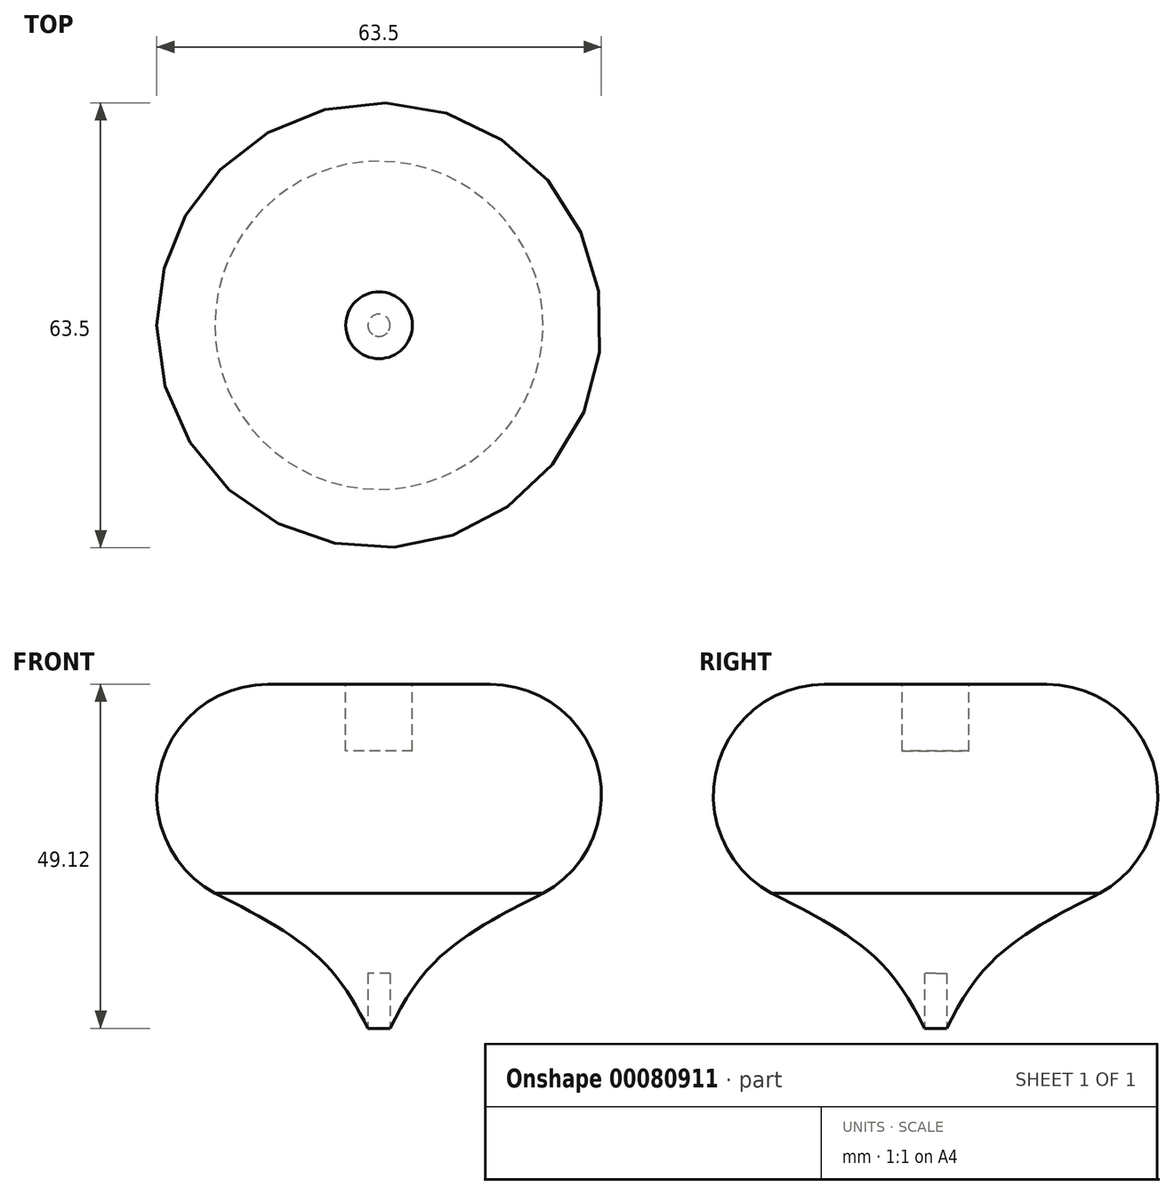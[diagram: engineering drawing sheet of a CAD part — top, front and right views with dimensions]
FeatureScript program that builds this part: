
annotation { "Feature Type Name" : "Feature", "Feature Type Description" : "" }
export const myFeature = defineFeature(function(context is Context, id is Id, definition is map)
    precondition{}
    {
        {
            var Q0;
            Q0=qCreatedBy(makeId("Right.planeOp"),FACE);
            var sketch = newSketch(context, id + "F0", { "sketchPlane" : qUnion([Q0])});
            skFitSpline(sketch, "E0", {"points": [v(0, 11.11) * mm, v(7.94, 23.81) * mm, v(23.43, 33.66) * mm], "startDerivative": vector(13.7, 28.66) * mm, "endDerivative": vector(32.82, 16.67) * mm});
            skLineSegment(sketch, "E1", {"start": v(0, 11.11) * mm, "end": v(0, 63.5) * mm});
            skArc(sketch, "E2", {"start": v(15.87, 63.5) * mm, "mid": v(31.26, 51.52) * mm, "end": v(23.43, 33.66) * mm});
            skLineSegment(sketch, "E3", {"start": v(0, 63.5) * mm, "end": v(15.87, 63.5) * mm});
            skLineSegment(sketch, "E4", {"start": v(0, 11.11) * mm, "end": v(0, 0) * mm});
            skSolve(sketch);
        }
        {
            var Q0;
            Q0=makeQuery(id+"F0.imprint","IMPRINT",FACE,{"disambiguationData":[TD([[makeQuery(id+"F0.imprint","IMPRINT",EDGE,{"derivedFrom":sQuery(id+"F0.wireOp",EDGE,"E0")}),1.0]])]});
            var Q1;
            Q1=sQuery(id+"F0.wireOp",EDGE,"E1");
            revolve(context, id + "F1", {"entities" : qUnion([Q0]), "axis" : qUnion([Q1]), "revolveType" : RevolveType.FULL});
        }
        {
            var Q0;
            Q0=makeQuery(id+"F1.opRevolve","SWEPT_FACE",FACE,{"disambiguationData":[OSD([sQuery(id+"F0.wireOp",EDGE,"E3")])]});
            var sketch = newSketch(context, id + "F2", { "sketchPlane" : qUnion([Q0])});
            skCircle(sketch, "E5", {"center": v(0, 0) * mm, "radius": 4.76 * mm});
            skSolve(sketch);
        }
        {
            var Q0;
            Q0 = qSketchRegion(id + "F2", true);
            extrude(context, id + "F3", {"entities" : qUnion([Q0]), "operationType" : NewBodyOperationType.REMOVE, "oppositeDirection" : true, "depth" : 9.52 * mm});
        }
        {
            var Q0;
            Q0=qCreatedBy(makeId("Top.planeOp"),FACE);
            var sketch = newSketch(context, id + "F4", { "sketchPlane" : qUnion([Q0])});
            skCircle(sketch, "E6", {"center": v(0, 0) * mm, "radius": 1.59 * mm});
            skSolve(sketch);
        }
        {
            var Q0;
            Q0=makeQuery(id+"F4.imprint","IMPRINT",FACE,{"disambiguationData":[TD([[makeQuery(id+"F4.imprint","IMPRINT",EDGE,{"derivedFrom":sQuery(id+"F4.wireOp",EDGE,"E6")}),1.0]])]});
            extrude(context, id + "F5", {"entities" : qUnion([Q0]), "operationType" : NewBodyOperationType.REMOVE, "depth" : 22.22 * mm});
        }
    });
